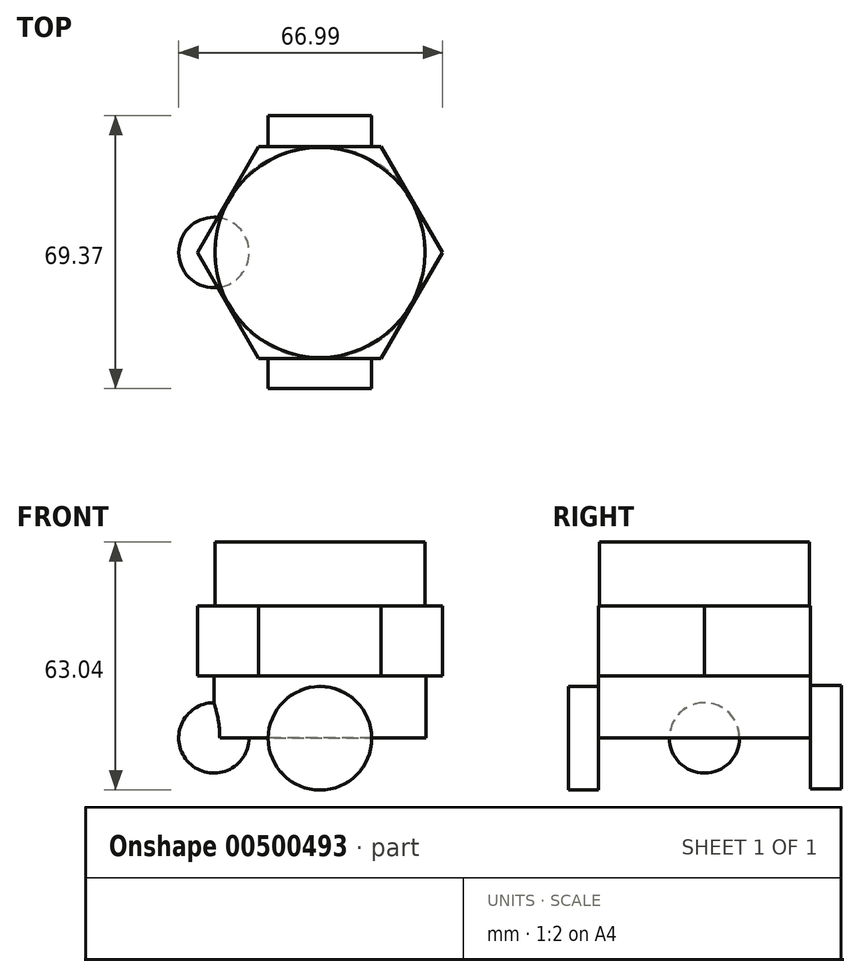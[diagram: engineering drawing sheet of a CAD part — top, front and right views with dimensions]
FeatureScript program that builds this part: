
annotation { "Feature Type Name" : "Feature", "Feature Type Description" : "" }
export const myFeature = defineFeature(function(context is Context, id is Id, definition is map)
    precondition{}
    {
        {
            var Q0;
            Q0=qCreatedBy(makeId("Top.planeOp"),FACE);
            var sketch = newSketch(context, id + "F0", { "sketchPlane" : qUnion([Q0])});
            skCircle(sketch, "E0", {"center": v(0, 0) * mm, "radius": 26.67 * mm});
            skSolve(sketch);
        }
        {
            var Q0;
            Q0=makeQuery(id+"F0.imprint","IMPRINT",FACE,{"disambiguationData":[TD([[makeQuery(id+"F0.imprint","IMPRINT",EDGE,{"derivedFrom":sQuery(id+"F0.wireOp",EDGE,"E0")}),1.0]])]});
            extrude(context, id + "F1", {"entities" : qUnion([Q0]), "depth" : 16.26 * mm});
        }
        {
            var Q0;
            Q0=qCreatedBy(makeId("Top.planeOp"),FACE);
            var sketch = newSketch(context, id + "F2", { "sketchPlane" : qUnion([Q0])});
            skCircle(sketch, "E1.cCircle", {"center": v(0, 0) * mm, "radius": 26.94 * mm, "construction": true});
            skLineSegment(sketch, "E1.0", {"start": v(-15.55, 26.94) * mm, "end": v(15.55, 26.94) * mm});
            skLineSegment(sketch, "E1.1", {"start": v(15.55, 26.94) * mm, "end": v(31.1, 0) * mm});
            skLineSegment(sketch, "E1.2", {"start": v(31.1, 0) * mm, "end": v(15.55, -26.94) * mm});
            skLineSegment(sketch, "E1.3", {"start": v(15.55, -26.94) * mm, "end": v(-15.55, -26.94) * mm});
            skLineSegment(sketch, "E1.4", {"start": v(-15.55, -26.94) * mm, "end": v(-31.1, 0) * mm});
            skLineSegment(sketch, "E1.5", {"start": v(-31.1, 0) * mm, "end": v(-15.55, 26.94) * mm});
            skPoint(sketch, "E1.0.midPoint", {"position": v(0, 26.94) * mm});
            skSolve(sketch);
        }
        {
            var Q0;
            Q0=makeQuery(id+"F2.imprint","IMPRINT",FACE,{"disambiguationData":[TD([[makeQuery(id+"F2.imprint","IMPRINT",EDGE,{"derivedFrom":sQuery(id+"F2.wireOp",EDGE,"E1.0")}),-1.0]])]});
            extrude(context, id + "F3", {"entities" : qUnion([Q0]), "operationType" : NewBodyOperationType.ADD, "oppositeDirection" : true, "depth" : 17.78 * mm});
        }
        {
            var Q0;
            Q0=makeQuery(id+"F3.opExtrude","CAP_FACE",FACE,{"disambiguationData":[OSD([sQuery(id+"F2.wireOp",EDGE,"E1.0"),sQuery(id+"F2.wireOp",EDGE,"E1.1"),sQuery(id+"F2.wireOp",EDGE,"E1.2"),sQuery(id+"F2.wireOp",EDGE,"E1.3"),sQuery(id+"F2.wireOp",EDGE,"E1.4"),sQuery(id+"F2.wireOp",EDGE,"E1.5")])],"isStart":false});
            var sketch = newSketch(context, id + "F4", { "sketchPlane" : qUnion([Q0])});
            skCircle(sketch, "E2", {"center": v(0, 0) * mm, "radius": 26.94 * mm});
            skSolve(sketch);
        }
        {
            var Q0;
            {var subQ0=sQuery(id+"F4.wireOp",EDGE,"E2");var subQ4=makeQuery(id+"F4.imprint","INTERSECT",VERTEX,{"derivedFrom":[makeQuery(id+"F3.opExtrude","CAP_EDGE",EDGE,{"disambiguationData":[OSD([sQuery(id+"F2.wireOp",EDGE,"E1.3")])],"isStart":false}),subQ0]});Q0=makeQuery(id+"F4.imprint","IMPRINT",FACE,{"disambiguationData":[TD([[makeQuery(id+"F4.imprint","IMPRINT",EDGE,{"disambiguationData":[TD([[subQ4,1.0]])],"derivedFrom":subQ0}),1.0]])]});}
            extrude(context, id + "F5", {"entities" : qUnion([Q0]), "operationType" : NewBodyOperationType.ADD, "depth" : 15.75 * mm});
        }
        {
            var Q0;
            Q0=makeQuery(id+"F3.opExtrude","SWEPT_FACE",FACE,{"disambiguationData":[OSD([sQuery(id+"F2.wireOp",EDGE,"E1.0")])]});
            var sketch = newSketch(context, id + "F6", { "sketchPlane" : qUnion([Q0])});
            skCircle(sketch, "E3", {"center": v(0, -33.37) * mm, "radius": 13.14 * mm});
            skSolve(sketch);
        }
        {
            var Q0;
            Q0 = qSketchRegion(id + "F6", true);
            extrude(context, id + "F7", {"entities" : qUnion([Q0]), "operationType" : NewBodyOperationType.ADD, "depth" : 7.87 * mm});
        }
        {
            var Q0;
            Q0=makeQuery(id+"F3.opExtrude","SWEPT_FACE",FACE,{"disambiguationData":[OSD([sQuery(id+"F2.wireOp",EDGE,"E1.3")])]});
            var sketch = newSketch(context, id + "F8", { "sketchPlane" : qUnion([Q0])});
            skCircle(sketch, "E4", {"center": v(0, -33.64) * mm, "radius": 13.14 * mm});
            skSolve(sketch);
        }
        {
            var Q0;
            Q0=makeQuery(id+"F8.imprint","IMPRINT",FACE,{"disambiguationData":[TD([[makeQuery(id+"F8.imprint","IMPRINT",EDGE,{"derivedFrom":sQuery(id+"F8.wireOp",EDGE,"E4")}),1.0]])]});
            extrude(context, id + "F9", {"entities" : qUnion([Q0]), "operationType" : NewBodyOperationType.ADD, "depth" : 7.62 * mm});
        }
        {
            var Q0;
            Q0=qCreatedBy(makeId("Top.planeOp"),FACE);
            var sketch = newSketch(context, id + "F10", { "sketchPlane" : qUnion([Q0])});
            skArc(sketch, "E5", {"start": v(0, 6.2) * mm, "mid": v(-6.2, 0) * mm, "end": v(0, -6.2) * mm});
            skLineSegment(sketch, "E6", {"start": v(0, 6.2) * mm, "end": v(0, -6.2) * mm});
            skSolve(sketch);
        }
        {
            var Q0;
            Q0=sQuery(id+"F10.wireOp",EDGE,"E5");
            var Q1;
            Q1=sQuery(id+"F10.wireOp",EDGE,"E6");
            revolve(context, id + "F11", {"bodyType" : ToolBodyType.SURFACE, "surfaceEntities" : qUnion([Q0]), "axis" : qUnion([Q1]), "revolveType" : RevolveType.FULL});
        }
        {
            var Q0;
            Q0=makeQuery(id+"F5.opExtrude","CAP_FACE",FACE,{"disambiguationData":[OSD([sQuery(id+"F4.wireOp",EDGE,"E2")])],"isStart":false});
            var sketch = newSketch(context, id + "F12", { "sketchPlane" : qUnion([Q0])});
            skArc(sketch, "E7", {"start": v(-26.94, 8.94) * mm, "mid": v(-35.88, 0) * mm, "end": v(-26.94, -8.94) * mm});
            skLineSegment(sketch, "E8", {"start": v(-26.94, 8.94) * mm, "end": v(-26.94, -8.94) * mm});
            skSolve(sketch);
        }
        {
            var Q0;
            {var subQ0=sQuery(id+"F12.wireOp",EDGE,"E7");Q0=makeQuery(id+"F12.imprint","IMPRINT",FACE,{"disambiguationData":[TD([[makeQuery(id+"F12.imprint","IMPRINT",EDGE,{"derivedFrom":subQ0}),1.0]])]});}
            var Q1;
            Q1=sQuery(id+"F12.wireOp",EDGE,"E8");
            revolve(context, id + "F13", {"operationType" : NewBodyOperationType.ADD, "entities" : qUnion([Q0]), "axis" : qUnion([Q1]), "revolveType" : RevolveType.FULL});
        }
    });
